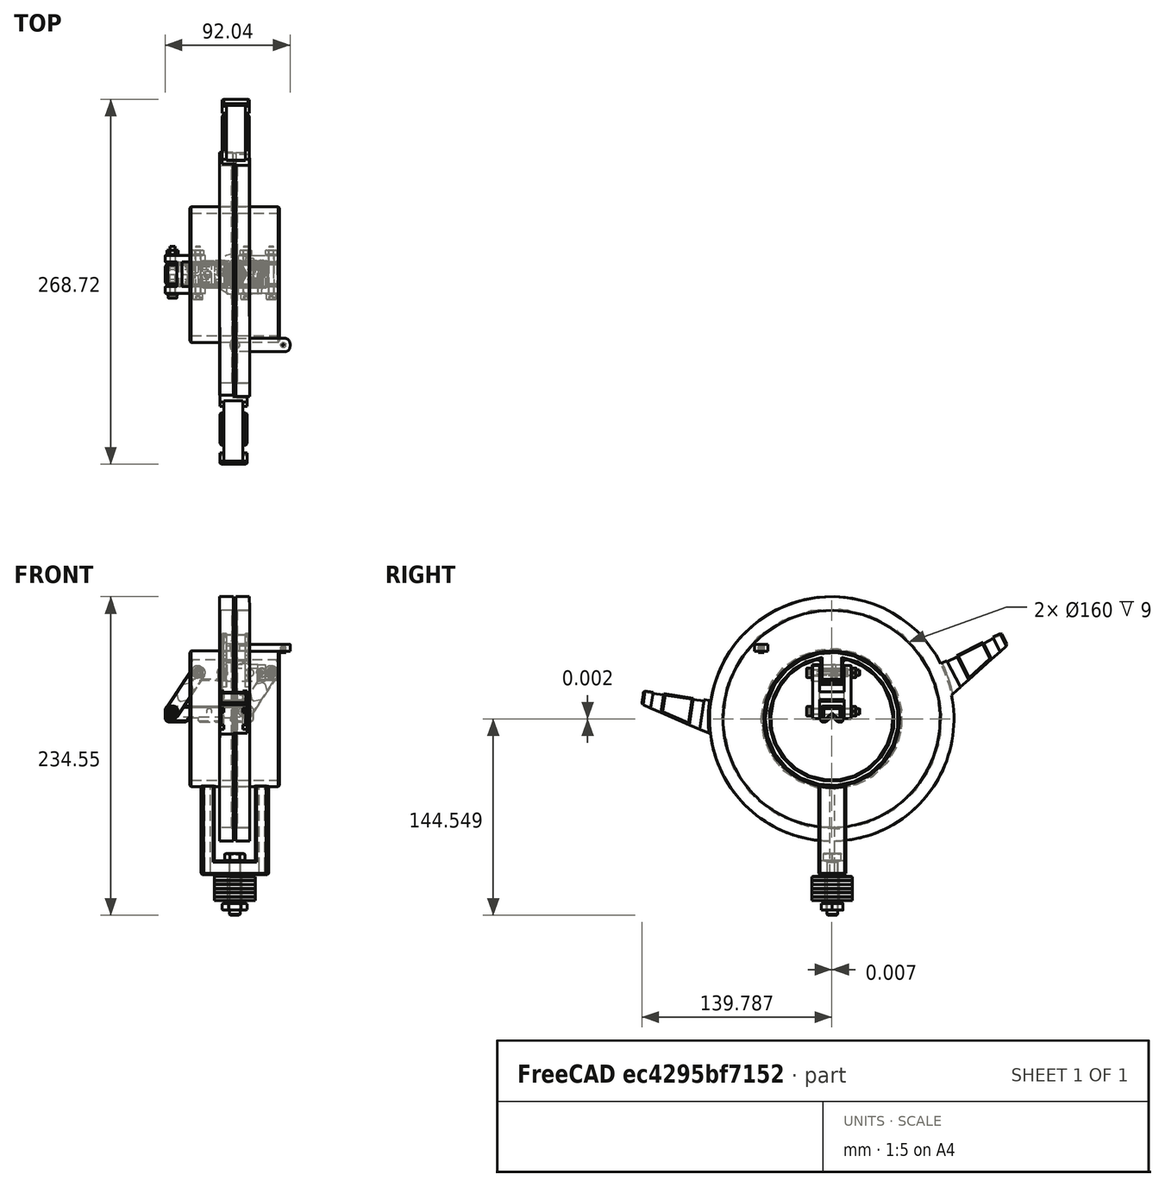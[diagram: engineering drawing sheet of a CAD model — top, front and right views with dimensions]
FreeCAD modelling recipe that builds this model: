
FCSTD DOCUMENT  (FreeCAD 0.18.3R)
Label: assenmbly
License: All rights reserved
LicenseURL: http://en.wikipedia.org/wiki/All_rights_reserved
objects: Part::FeaturePython×45, App::FeaturePython×40
note: 45 computed .brp shape members not serialized (recipe doc carries the construction recipe); baked Part::Feature solids carry a one-line shape summary decoded from their .brp

FEATURE [Part::FeaturePython] b_schlitten_001_  label="schlitten_001"  # a2plus imported part (geometry in sourceFile) (typed FeaturePython)
  Placement = pos=(-61.9458,5.97392,0.234447) rot=(0,0,1;0rad)
  a2p_Version = V0.1
  fixedPosition = true
  sourceFile = ./schlitten.FCStd
  subassemblyImport = false
  timeLastImport = 1.57901e+09
  updateColors = true
FEATURE [Part::FeaturePython] b_hinge_001_  label="hinge_001"  # a2plus imported part (geometry in sourceFile) (typed FeaturePython)
  Placement = pos=(-83.7786,5.97392,25.1844) rot=(-0.66073,0.66073,-0.356189;2.45724rad)
  a2p_Version = V0.1
  fixedPosition = false
  sourceFile = ./hinge.FCStd
  subassemblyImport = false
  timeLastImport = 1.57901e+09
  updateColors = true
FEATURE [Part::FeaturePython] b_uscheibe_001_  label="uscheibe_001"  # a2plus imported part (geometry in sourceFile) (typed FeaturePython)
  Placement = pos=(-34.9458,14.9739,8.23445) rot=(1,0,0;1.5708rad)
  a2p_Version = V0.1
  fixedPosition = false
  sourceFile = ./uscheibe.FCStd
  subassemblyImport = false
  timeLastImport = 1.57901e+09
  updateColors = true
FEATURE [Part::FeaturePython] b_uscheibe_001_001  label="uscheibe_002"  # a2plus imported part (geometry in sourceFile) (typed FeaturePython)
  Placement = pos=(-88.9458,14.9739,8.23445) rot=(0.998298,0.041235,-0.041235;1.5725rad)
  a2p_Version = V0.1
  fixedPosition = false
  sourceFile = ./uscheibe.FCStd
  subassemblyImport = false
  timeLastImport = 1.57901e+09
  updateColors = true
FEATURE [App::FeaturePython] circularEdge_001  label="circularEdge_001__schlitten_001"  # a2plus constraint (typed FeaturePython)
  Object1 = b_uscheibe_001_001
  Object2 = b_schlitten_001_
  ParentTreeObject = -> b_uscheibe_001_001
  SubElement1 = Edge6
  SubElement2 = Edge59
  Type = circularEdge
  directionConstraint = 1
  lockRotation = false
  offset = 0
FEATURE [App::FeaturePython] circularEdge_001_mirror  label="circularEdge_001__uscheibe_002"  # a2plus constraint (typed FeaturePython)
  Object1 = b_uscheibe_001_001
  Object2 = b_schlitten_001_
  ParentTreeObject = -> b_schlitten_001_
  SubElement1 = Edge6
  SubElement2 = Edge59
  Type = circularEdge
  directionConstraint = 1
  lockRotation = false
  offset = 0
FEATURE [App::FeaturePython] circularEdge_002  label="circularEdge_002__uscheibe_002"  # a2plus constraint (typed FeaturePython)
  Object1 = b_hinge_001_
  Object2 = b_uscheibe_001_001
  ParentTreeObject = -> b_hinge_001_
  SubElement1 = Edge11
  SubElement2 = Edge5
  Type = circularEdge
  directionConstraint = 0
  lockRotation = false
  offset = 0
FEATURE [App::FeaturePython] circularEdge_002_mirror  label="circularEdge_002__hinge_001"  # a2plus constraint (typed FeaturePython)
  Object1 = b_hinge_001_
  Object2 = b_uscheibe_001_001
  ParentTreeObject = -> b_uscheibe_001_001
  SubElement1 = Edge11
  SubElement2 = Edge5
  Type = circularEdge
  directionConstraint = 0
  lockRotation = false
  offset = 0
FEATURE [App::FeaturePython] circularEdge_003  label="circularEdge_003__schlitten_001"  # a2plus constraint (typed FeaturePython)
  Object1 = b_uscheibe_001_
  Object2 = b_schlitten_001_
  ParentTreeObject = -> b_uscheibe_001_
  SubElement1 = Edge6
  SubElement2 = Edge63
  Type = circularEdge
  directionConstraint = 1
  lockRotation = false
  offset = 0
FEATURE [App::FeaturePython] circularEdge_003_mirror  label="circularEdge_003__uscheibe_001"  # a2plus constraint (typed FeaturePython)
  Object1 = b_uscheibe_001_
  Object2 = b_schlitten_001_
  ParentTreeObject = -> b_schlitten_001_
  SubElement1 = Edge6
  SubElement2 = Edge63
  Type = circularEdge
  directionConstraint = 1
  lockRotation = false
  offset = 0
FEATURE [Part::FeaturePython] b_uscheibe_001_002  label="uscheibe_003"  # a2plus imported part (geometry in sourceFile) (typed FeaturePython)
  Placement = pos=(-34.9458,-2.02608,8.23445) rot=(0.996711,-0.057304,0.057304;1.57409rad)
  a2p_Version = V0.1
  fixedPosition = false
  sourceFile = ./uscheibe.FCStd
  subassemblyImport = false
  timeLastImport = 1.57901e+09
  updateColors = true
FEATURE [Part::FeaturePython] b_uscheibe_001_003  label="uscheibe_004"  # a2plus imported part (geometry in sourceFile) (typed FeaturePython)
  Placement = pos=(-88.9458,-2.02608,8.23445) rot=(1,0,0;1.5708rad)
  a2p_Version = V0.1
  fixedPosition = false
  sourceFile = ./uscheibe.FCStd
  subassemblyImport = false
  timeLastImport = 1.57901e+09
  updateColors = true
FEATURE [App::FeaturePython] circularEdge_004  label="circularEdge_004__schlitten_001"  # a2plus constraint (typed FeaturePython)
  Object1 = b_uscheibe_001_003
  Object2 = b_schlitten_001_
  ParentTreeObject = -> b_uscheibe_001_003
  SubElement1 = Edge5
  SubElement2 = Edge15
  Type = circularEdge
  directionConstraint = 1
  lockRotation = false
  offset = 0
FEATURE [App::FeaturePython] circularEdge_004_mirror  label="circularEdge_004__uscheibe_004"  # a2plus constraint (typed FeaturePython)
  Object1 = b_uscheibe_001_003
  Object2 = b_schlitten_001_
  ParentTreeObject = -> b_schlitten_001_
  SubElement1 = Edge5
  SubElement2 = Edge15
  Type = circularEdge
  directionConstraint = 1
  lockRotation = false
  offset = 0
FEATURE [App::FeaturePython] circularEdge_005  label="circularEdge_005__schlitten_001"  # a2plus constraint (typed FeaturePython)
  Object1 = b_uscheibe_001_002
  Object2 = b_schlitten_001_
  ParentTreeObject = -> b_uscheibe_001_002
  SubElement1 = Edge5
  SubElement2 = Edge17
  Type = circularEdge
  directionConstraint = 1
  lockRotation = false
  offset = 0
FEATURE [App::FeaturePython] circularEdge_005_mirror  label="circularEdge_005__uscheibe_003"  # a2plus constraint (typed FeaturePython)
  Object1 = b_uscheibe_001_002
  Object2 = b_schlitten_001_
  ParentTreeObject = -> b_schlitten_001_
  SubElement1 = Edge5
  SubElement2 = Edge17
  Type = circularEdge
  directionConstraint = 1
  lockRotation = false
  offset = 0
FEATURE [Part::FeaturePython] b_hinge_001_001  label="hinge_002"  # a2plus imported part (geometry in sourceFile) (typed FeaturePython)
  Placement = pos=(-21.4247,5.97392,19.6879) rot=(0.428706,-0.428706,-0.79525;1.79792rad)
  a2p_Version = V0.1
  fixedPosition = false
  sourceFile = ./hinge.FCStd
  subassemblyImport = false
  timeLastImport = 1.57901e+09
  updateColors = true
FEATURE [App::FeaturePython] circularEdge_006  label="circularEdge_006__uscheibe_003"  # a2plus constraint (typed FeaturePython)
  Object1 = b_hinge_001_001
  Object2 = b_uscheibe_001_002
  ParentTreeObject = -> b_hinge_001_001
  SubElement1 = Edge84
  SubElement2 = Edge6
  Type = circularEdge
  directionConstraint = 0
  lockRotation = false
  offset = 0
FEATURE [App::FeaturePython] circularEdge_006_mirror  label="circularEdge_006__hinge_002"  # a2plus constraint (typed FeaturePython)
  Object1 = b_hinge_001_001
  Object2 = b_uscheibe_001_002
  ParentTreeObject = -> b_uscheibe_001_002
  SubElement1 = Edge84
  SubElement2 = Edge6
  Type = circularEdge
  directionConstraint = 0
  lockRotation = false
  offset = 0
FEATURE [Part::FeaturePython] b_uscheibe_001_004  label="uscheibe_005"  # a2plus imported part (geometry in sourceFile) (typed FeaturePython)
  Placement = pos=(-70.2575,13.9739,36.6378) rot=(-0.243331,0.685853,0.685853;2.66421rad)
  a2p_Version = V0.1
  fixedPosition = false
  sourceFile = ./uscheibe.FCStd
  subassemblyImport = false
  timeLastImport = 1.57901e+09
  updateColors = true
FEATURE [Part::FeaturePython] b_uscheibe_001_005  label="uscheibe_006"  # a2plus imported part (geometry in sourceFile) (typed FeaturePython)
  Placement = pos=(-16.2575,13.9739,36.6378) rot=(0.393172,0.65016,0.65016;3.89081rad)
  a2p_Version = V0.1
  fixedPosition = false
  sourceFile = ./uscheibe.FCStd
  subassemblyImport = false
  timeLastImport = 1.57901e+09
  updateColors = true
FEATURE [Part::FeaturePython] b_uscheibe_001_006  label="uscheibe_007"  # a2plus imported part (geometry in sourceFile) (typed FeaturePython)
  Placement = pos=(-70.2575,-2.02608,36.6378) rot=(0.99737,0.051246,-0.051246;1.57343rad)
  a2p_Version = V0.1
  fixedPosition = false
  sourceFile = ./uscheibe.FCStd
  subassemblyImport = false
  timeLastImport = 1.57901e+09
  updateColors = true
FEATURE [Part::FeaturePython] b_uscheibe_001_007  label="uscheibe_008"  # a2plus imported part (geometry in sourceFile) (typed FeaturePython)
  Placement = pos=(-16.2575,-2.02608,36.6378) rot=(0.996759,-0.056884,0.056884;1.57404rad)
  a2p_Version = V0.1
  fixedPosition = false
  sourceFile = ./uscheibe.FCStd
  subassemblyImport = false
  timeLastImport = 1.57901e+09
  updateColors = true
FEATURE [App::FeaturePython] circularEdge_007  label="circularEdge_007__hinge_001"  # a2plus constraint (typed FeaturePython)
  Object1 = b_uscheibe_001_004
  Object2 = b_hinge_001_
  ParentTreeObject = -> b_uscheibe_001_004
  SubElement1 = Edge6
  SubElement2 = Edge67
  Type = circularEdge
  directionConstraint = 1
  lockRotation = false
  offset = 0
FEATURE [App::FeaturePython] circularEdge_007_mirror  label="circularEdge_007__uscheibe_005"  # a2plus constraint (typed FeaturePython)
  Object1 = b_uscheibe_001_004
  Object2 = b_hinge_001_
  ParentTreeObject = -> b_hinge_001_
  SubElement1 = Edge6
  SubElement2 = Edge67
  Type = circularEdge
  directionConstraint = 1
  lockRotation = false
  offset = 0
FEATURE [App::FeaturePython] circularEdge_008  label="circularEdge_008__hinge_002"  # a2plus constraint (typed FeaturePython)
  Object1 = b_uscheibe_001_005
  Object2 = b_hinge_001_001
  ParentTreeObject = -> b_uscheibe_001_005
  SubElement1 = Edge6
  SubElement2 = Edge11
  Type = circularEdge
  directionConstraint = 1
  lockRotation = false
  offset = 0
FEATURE [App::FeaturePython] circularEdge_008_mirror  label="circularEdge_008__uscheibe_006"  # a2plus constraint (typed FeaturePython)
  Object1 = b_uscheibe_001_005
  Object2 = b_hinge_001_001
  ParentTreeObject = -> b_hinge_001_001
  SubElement1 = Edge6
  SubElement2 = Edge11
  Type = circularEdge
  directionConstraint = 1
  lockRotation = false
  offset = 0
FEATURE [App::FeaturePython] circularEdge_009  label="circularEdge_009__hinge_001"  # a2plus constraint (typed FeaturePython)
  Object1 = b_uscheibe_001_006
  Object2 = b_hinge_001_
  ParentTreeObject = -> b_uscheibe_001_006
  SubElement1 = Edge6
  SubElement2 = Edge84
  Type = circularEdge
  directionConstraint = 0
  lockRotation = false
  offset = 0
FEATURE [App::FeaturePython] circularEdge_009_mirror  label="circularEdge_009__uscheibe_007"  # a2plus constraint (typed FeaturePython)
  Object1 = b_uscheibe_001_006
  Object2 = b_hinge_001_
  ParentTreeObject = -> b_hinge_001_
  SubElement1 = Edge6
  SubElement2 = Edge84
  Type = circularEdge
  directionConstraint = 0
  lockRotation = false
  offset = 0
FEATURE [App::FeaturePython] circularEdge_010  label="circularEdge_010__hinge_002"  # a2plus constraint (typed FeaturePython)
  Object1 = b_uscheibe_001_007
  Object2 = b_hinge_001_001
  ParentTreeObject = -> b_uscheibe_001_007
  SubElement1 = Edge6
  SubElement2 = Edge61
  Type = circularEdge
  directionConstraint = 0
  lockRotation = false
  offset = 0
FEATURE [App::FeaturePython] circularEdge_010_mirror  label="circularEdge_010__uscheibe_008"  # a2plus constraint (typed FeaturePython)
  Object1 = b_uscheibe_001_007
  Object2 = b_hinge_001_001
  ParentTreeObject = -> b_hinge_001_001
  SubElement1 = Edge6
  SubElement2 = Edge61
  Type = circularEdge
  directionConstraint = 0
  lockRotation = false
  offset = 0
FEATURE [Part::FeaturePython] b_gondel_001_  label="gondel_001"  # a2plus imported part (geometry in sourceFile) (typed FeaturePython)
  Placement = pos=(-43.2575,5.87277,2.6378) rot=(0.57735,-0.57735,-0.57735;2.0944rad)
  a2p_Version = V0.1
  fixedPosition = false
  sourceFile = ./gondel.FCStd
  subassemblyImport = false
  timeLastImport = 1.57901e+09
  updateColors = true
FEATURE [App::FeaturePython] circularEdge_011  label="circularEdge_011__gondel_001"  # a2plus constraint (typed FeaturePython)
  Object1 = b_uscheibe_001_006
  Object2 = b_gondel_001_
  ParentTreeObject = -> b_uscheibe_001_006
  SubElement1 = Edge5
  SubElement2 = Edge68
  Type = circularEdge
  directionConstraint = 0
  lockRotation = false
  offset = 0
FEATURE [App::FeaturePython] circularEdge_011_mirror  label="circularEdge_011__uscheibe_007"  # a2plus constraint (typed FeaturePython)
  Object1 = b_uscheibe_001_006
  Object2 = b_gondel_001_
  ParentTreeObject = -> b_gondel_001_
  SubElement1 = Edge5
  SubElement2 = Edge68
  Type = circularEdge
  directionConstraint = 0
  lockRotation = false
  offset = 0
FEATURE [App::FeaturePython] circularEdge_012  label="circularEdge_012__uscheibe_008"  # a2plus constraint (typed FeaturePython)
  Object1 = b_gondel_001_
  Object2 = b_uscheibe_001_007
  ParentTreeObject = -> b_gondel_001_
  SubElement1 = Edge66
  SubElement2 = Edge5
  Type = circularEdge
  directionConstraint = 0
  lockRotation = false
  offset = 0
FEATURE [App::FeaturePython] circularEdge_012_mirror  label="circularEdge_012__gondel_001"  # a2plus constraint (typed FeaturePython)
  Object1 = b_gondel_001_
  Object2 = b_uscheibe_001_007
  ParentTreeObject = -> b_uscheibe_001_007
  SubElement1 = Edge66
  SubElement2 = Edge5
  Type = circularEdge
  directionConstraint = 0
  lockRotation = false
  offset = 0
FEATURE [App::FeaturePython] circularEdge_013  label="circularEdge_013__uscheibe_008"  # a2plus constraint (typed FeaturePython)
  Object1 = b_hinge_001_001
  Object2 = b_uscheibe_001_007
  ParentTreeObject = -> b_hinge_001_001
  SubElement1 = Edge61
  SubElement2 = Edge6
  Type = circularEdge
  directionConstraint = 0
  lockRotation = false
  offset = 0
FEATURE [App::FeaturePython] circularEdge_013_mirror  label="circularEdge_013__hinge_002"  # a2plus constraint (typed FeaturePython)
  Object1 = b_hinge_001_001
  Object2 = b_uscheibe_001_007
  ParentTreeObject = -> b_uscheibe_001_007
  SubElement1 = Edge61
  SubElement2 = Edge6
  Type = circularEdge
  directionConstraint = 0
  lockRotation = false
  offset = 0
FEATURE [Part::FeaturePython] b_servo_001_  label="servo_001"  # a2plus imported part (geometry in sourceFile) (typed FeaturePython)
  Placement = pos=(-32.0813,-8.31554,36.6357) rot=(-0.99997,-0.005509,0.005531;1.5707rad)
  a2p_Version = V0.1
  fixedPosition = false
  sourceFile = ./servo.FCStd
  subassemblyImport = false
  timeLastImport = 1.57901e+09
  updateColors = true
FEATURE [App::FeaturePython] circularEdge_014  label="circularEdge_014__gondel_001"  # a2plus constraint (typed FeaturePython)
  Object1 = b_servo_001_
  Object2 = b_gondel_001_
  ParentTreeObject = -> b_servo_001_
  SubElement1 = Edge64
  SubElement2 = Edge137
  Type = circularEdge
  directionConstraint = 1
  lockRotation = false
  offset = 0
FEATURE [App::FeaturePython] circularEdge_014_mirror  label="circularEdge_014__servo_001"  # a2plus constraint (typed FeaturePython)
  Object1 = b_servo_001_
  Object2 = b_gondel_001_
  ParentTreeObject = -> b_gondel_001_
  SubElement1 = Edge64
  SubElement2 = Edge137
  Type = circularEdge
  directionConstraint = 1
  lockRotation = false
  offset = 0
FEATURE [App::FeaturePython] circularEdge_015  label="circularEdge_015__servo_001"  # a2plus constraint (typed FeaturePython)
  Object1 = b_gondel_001_
  Object2 = b_servo_001_
  ParentTreeObject = -> b_gondel_001_
  SubElement1 = Edge106
  SubElement2 = Edge58
  Type = circularEdge
  directionConstraint = 1
  lockRotation = false
  offset = 0
FEATURE [App::FeaturePython] circularEdge_015_mirror  label="circularEdge_015__gondel_001"  # a2plus constraint (typed FeaturePython)
  Object1 = b_gondel_001_
  Object2 = b_servo_001_
  ParentTreeObject = -> b_servo_001_
  SubElement1 = Edge106
  SubElement2 = Edge58
  Type = circularEdge
  directionConstraint = 1
  lockRotation = false
  offset = 0
FEATURE [Part::FeaturePython] Washer002  label="M4-Washer105"  # Fasteners workbench fastener (typed FeaturePython)
  Placement = pos=(-88.9458,-8.02608,8.23445) rot=(1,0,0;1.5708rad)
  baseObject = -> b_hinge_001_ [Edge77]
  diameter = 5
  invert = false
  matchOuter = false
  offset = 0
  type = 2
FEATURE [Part::FeaturePython] Washer003  label="M4-Washer103"  # Fasteners workbench fastener (typed FeaturePython)
  Placement = pos=(-34.9458,-8.02608,8.23445) rot=(1,0,0;1.5708rad)
  baseObject = -> b_hinge_001_001 [Edge78]
  diameter = 5
  invert = false
  matchOuter = false
  offset = 0
  type = 2
FEATURE [Part::FeaturePython] Washer004  label="M4-Washer100"  # Fasteners workbench fastener (typed FeaturePython)
  Placement = pos=(-88.9458,19.9739,8.23445) rot=(-1,0,0;1.5708rad)
  baseObject = -> b_hinge_001_ [Edge51]
  diameter = 5
  invert = true
  matchOuter = false
  offset = 0
  type = 2
FEATURE [Part::FeaturePython] Washer005  label="M4-Washer102"  # Fasteners workbench fastener (typed FeaturePython)
  Placement = pos=(-34.9458,19.9739,8.23445) rot=(-1,0,0;1.5708rad)
  baseObject = -> b_hinge_001_001 [Edge55]
  diameter = 5
  invert = true
  matchOuter = false
  offset = 0
  type = 2
FEATURE [Part::FeaturePython] Washer  label="M4-Washer101"  # Fasteners workbench fastener (typed FeaturePython)
  Placement = pos=(-16.2575,19.9739,36.6378) rot=(-1,0,0;1.5708rad)
  baseObject = -> b_hinge_001_001 [Edge51]
  diameter = 5
  invert = true
  matchOuter = false
  offset = 0
  type = 2
FEATURE [Part::FeaturePython] Washer006  label="M4-Washer099"  # Fasteners workbench fastener (typed FeaturePython)
  Placement = pos=(-70.2575,19.9739,36.6378) rot=(-1,0,0;1.5708rad)
  baseObject = -> b_hinge_001_ [Edge55]
  diameter = 5
  invert = true
  matchOuter = false
  offset = 0
  type = 2
FEATURE [Part::FeaturePython] Washer007  label="M4-Washer"  # Fasteners workbench fastener (typed FeaturePython)
  Placement = pos=(-16.2575,-8.02608,36.6378) rot=(1,0,0;1.5708rad)
  baseObject = -> b_hinge_001_001 [Edge77]
  diameter = 5
  invert = false
  matchOuter = false
  offset = 0
  type = 2
FEATURE [Part::FeaturePython] Washer008  label="M4-Washer104"  # Fasteners workbench fastener (typed FeaturePython)
  Placement = pos=(-70.2575,-8.02608,36.6378) rot=(1,0,0;1.5708rad)
  baseObject = -> b_hinge_001_ [Edge78]
  diameter = 5
  invert = false
  matchOuter = false
  offset = 0
  type = 2
FEATURE [Part::FeaturePython] Screw  label="M4x35-Screw045"  # Fasteners workbench fastener (typed FeaturePython)
  Placement = pos=(-88.9458,-8.57608,8.23445) rot=(1,0,0;1.5708rad)
  baseObject = -> Washer002 [Edge1]
  diameter = 5
  invert = false
  length = 10
  matchOuter = false
  offset = 0
  thread = false
  type = 6
FEATURE [Part::FeaturePython] Screw001  label="M4x35-Screw044"  # Fasteners workbench fastener (typed FeaturePython)
  Placement = pos=(-70.2575,-8.57608,36.6378) rot=(1,0,0;1.5708rad)
  baseObject = -> Washer008 [Edge1]
  diameter = 4
  invert = false
  length = 8
  matchOuter = false
  offset = 0
  thread = false
  type = 5
FEATURE [Part::FeaturePython] Screw002  label="M4x35-Screw"  # Fasteners workbench fastener (typed FeaturePython)
  Placement = pos=(-34.9458,-8.57608,8.23445) rot=(1,0,0;1.5708rad)
  baseObject = -> Washer003 [Edge1]
  diameter = 4
  invert = false
  length = 8
  matchOuter = false
  offset = 0
  thread = false
  type = 5
FEATURE [Part::FeaturePython] Screw003  label="M4x35-Screw043"  # Fasteners workbench fastener (typed FeaturePython)
  Placement = pos=(-16.2575,-8.57608,36.6378) rot=(1,0,0;1.5708rad)
  baseObject = -> Washer007 [Edge1]
  diameter = 4
  invert = false
  length = 8
  matchOuter = false
  offset = 0
  thread = false
  type = 5
FEATURE [Part::FeaturePython] Nut  label="M4-Nut"  # Fasteners workbench fastener (typed FeaturePython)
  Placement = pos=(-34.9458,20.5239,8.23445) rot=(-1,0,0;1.5708rad)
  baseObject = -> Washer005 [Edge1]
  diameter = 6
  invert = false
  matchOuter = false
  offset = 0
  thread = false
  type = 4
FEATURE [Part::FeaturePython] Nut001  label="M4-Nut045"  # Fasteners workbench fastener (typed FeaturePython)
  Placement = pos=(-16.2575,20.5239,36.6378) rot=(-1,0,0;1.5708rad)
  baseObject = -> Washer [Edge1]
  diameter = 6
  invert = false
  matchOuter = false
  offset = 0
  thread = false
  type = 4
FEATURE [Part::FeaturePython] Nut002  label="M4-Nut044"  # Fasteners workbench fastener (typed FeaturePython)
  Placement = pos=(-88.9458,20.5239,8.23445) rot=(-1,0,0;1.5708rad)
  baseObject = -> Washer004 [Edge1]
  diameter = 6
  invert = false
  matchOuter = false
  offset = 0
  thread = false
  type = 4
FEATURE [Part::FeaturePython] Nut003  label="M4-Nut043"  # Fasteners workbench fastener (typed FeaturePython)
  Placement = pos=(-70.2575,20.5239,36.6378) rot=(-1,0,0;1.5708rad)
  baseObject = -> Washer006 [Edge1]
  diameter = 6
  invert = false
  matchOuter = false
  offset = 0
  thread = false
  type = 4
FEATURE [Part::FeaturePython] Screw004  label="M3x4-Screw"  # Fasteners workbench fastener (typed FeaturePython)
  Placement = pos=(-52.2575,13.9739,36.6378) rot=(-1,0,0;1.5708rad)
  baseObject = -> b_gondel_001_ [Edge48]
  diameter = 1
  invert = true
  length = 0
  matchOuter = false
  offset = 0
  thread = false
  type = 0
FEATURE [Part::FeaturePython] Screw005  label="M3x4-Screw001"  # Fasteners workbench fastener (typed FeaturePython)
  Placement = pos=(-23.2575,13.9739,36.6378) rot=(-1,0,0;1.5708rad)
  baseObject = -> b_gondel_001_ [Edge46]
  diameter = 1
  invert = true
  length = 0
  matchOuter = false
  offset = 0
  thread = false
  type = 0
FEATURE [Part::FeaturePython] b_rotor_001_  label="rotor_001"  # a2plus imported part (geometry in sourceFile) (typed FeaturePython)
  Placement = pos=(-24.4097,-46.0942,52.5618) rot=(0,0,1;0rad)
  a2p_Version = V0.1
  fixedPosition = false
  sourceFile = ./rotor.FCStd
  subassemblyImport = false
  timeLastImport = 1.57901e+09
  updateColors = true
FEATURE [Part::FeaturePython] b_lager_001_  label="lager_001"  # a2plus imported part (geometry in sourceFile) (typed FeaturePython)
  Placement = pos=(16.7425,5.87277,2.6378) rot=(-0.570077,0.591629,-0.570077;2.07311rad)
  a2p_Version = V0.1
  fixedPosition = false
  sourceFile = ./lager.FCStd
  subassemblyImport = false
  timeLastImport = 1.579e+09
  updateColors = true
FEATURE [App::FeaturePython] circularEdge_016  label="circularEdge_016__gondel_001"  # a2plus constraint (typed FeaturePython)
  Object1 = b_lager_001_
  Object2 = b_gondel_001_
  ParentTreeObject = -> b_lager_001_
  SubElement1 = Edge8
  SubElement2 = Edge2
  Type = circularEdge
  directionConstraint = 1
  lockRotation = false
  offset = 0
FEATURE [App::FeaturePython] circularEdge_016_mirror  label="circularEdge_016__lager_001"  # a2plus constraint (typed FeaturePython)
  Object1 = b_lager_001_
  Object2 = b_gondel_001_
  ParentTreeObject = -> b_gondel_001_
  SubElement1 = Edge8
  SubElement2 = Edge2
  Type = circularEdge
  directionConstraint = 1
  lockRotation = false
  offset = 0
FEATURE [Part::FeaturePython] b_lager_001_001  label="lager_002"  # a2plus imported part (geometry in sourceFile) (typed FeaturePython)
  Placement = pos=(4.74247,5.87277,2.6378) rot=(-0.570077,0.591629,-0.570077;2.07311rad)
  a2p_Version = V0.1
  fixedPosition = false
  sourceFile = ./lager.FCStd
  subassemblyImport = false
  timeLastImport = 1.579e+09
  updateColors = true
FEATURE [App::FeaturePython] circularEdge_017  label="circularEdge_017__lager_002"  # a2plus constraint (typed FeaturePython)
  Object1 = b_gondel_001_
  Object2 = b_lager_001_001
  ParentTreeObject = -> b_gondel_001_
  SubElement1 = Edge12
  SubElement2 = Edge9
  Type = circularEdge
  directionConstraint = 1
  lockRotation = false
  offset = 0
FEATURE [App::FeaturePython] circularEdge_017_mirror  label="circularEdge_017__gondel_001"  # a2plus constraint (typed FeaturePython)
  Object1 = b_gondel_001_
  Object2 = b_lager_001_001
  ParentTreeObject = -> b_lager_001_001
  SubElement1 = Edge12
  SubElement2 = Edge9
  Type = circularEdge
  directionConstraint = 1
  lockRotation = false
  offset = 0
FEATURE [Part::FeaturePython] b_fluegel_001_  label="fluegel_001"  # a2plus imported part (geometry in sourceFile) (typed FeaturePython)
  Placement = pos=(-32.2575,5.87508,2.64019) rot=(-0.648745,0.398243,0.648485;3.89967rad)
  a2p_Version = V0.1
  fixedPosition = false
  sourceFile = ./fluegel.FCStd
  subassemblyImport = false
  timeLastImport = 1.57902e+09
  updateColors = true
FEATURE [App::FeaturePython] circularEdge_018  label="circularEdge_018__lager_001"  # a2plus constraint (typed FeaturePython)
  Object1 = b_fluegel_001_
  Object2 = b_lager_001_
  ParentTreeObject = -> b_fluegel_001_
  SubElement1 = Edge152
  SubElement2 = Edge2
  Type = circularEdge
  directionConstraint = 1
  lockRotation = false
  offset = 0
FEATURE [App::FeaturePython] circularEdge_018_mirror  label="circularEdge_018__fluegel_001"  # a2plus constraint (typed FeaturePython)
  Object1 = b_fluegel_001_
  Object2 = b_lager_001_
  ParentTreeObject = -> b_lager_001_
  SubElement1 = Edge152
  SubElement2 = Edge2
  Type = circularEdge
  directionConstraint = 1
  lockRotation = false
  offset = 0
FEATURE [Part::FeaturePython] b_fluegel_001_001  label="fluegel_002"  # a2plus imported part (geometry in sourceFile) (typed FeaturePython)
  Placement = pos=(-54.258,5.86198,2.6434) rot=(-0.545997,-0.635085,-0.546401;4.27173rad)
  a2p_Version = V0.1
  fixedPosition = false
  sourceFile = ./fluegel.FCStd
  subassemblyImport = false
  timeLastImport = 1.57902e+09
  updateColors = true
FEATURE [App::FeaturePython] circularEdge_019  label="circularEdge_019__lager_002"  # a2plus constraint (typed FeaturePython)
  Object1 = b_fluegel_001_001
  Object2 = b_lager_001_001
  ParentTreeObject = -> b_fluegel_001_001
  SubElement1 = Edge152
  SubElement2 = Edge3
  Type = circularEdge
  directionConstraint = 0
  lockRotation = false
  offset = 0
FEATURE [App::FeaturePython] circularEdge_019_mirror  label="circularEdge_019__fluegel_002"  # a2plus constraint (typed FeaturePython)
  Object1 = b_fluegel_001_001
  Object2 = b_lager_001_001
  ParentTreeObject = -> b_lager_001_001
  SubElement1 = Edge152
  SubElement2 = Edge3
  Type = circularEdge
  directionConstraint = 0
  lockRotation = false
  offset = 0
FEATURE [Part::FeaturePython] b_waage_001_  label="waage_001"  # a2plus imported part (geometry in sourceFile) (typed FeaturePython)
  Placement = pos=(-42.9356,6.17693,3.09831) rot=(0,1,0;1.57234rad)
  a2p_Version = V0.1
  fixedPosition = false
  sourceFile = ./waage.FCStd
  subassemblyImport = false
  timeLastImport = 1.57925e+09
  updateColors = true
FEATURE [App::FeaturePython] axisParallel_001  label="axisParallel_001__gondel_001"  # a2plus constraint (typed FeaturePython)
  Object1 = b_waage_001_
  Object2 = b_gondel_001_
  ParentTreeObject = -> b_waage_001_
  SubElement1 = Face13
  SubElement2 = Face13
  Type = axisParallel
  directionConstraint = 0
FEATURE [App::FeaturePython] axisParallel_001_mirror  label="axisParallel_001__waage_001"  # a2plus constraint (typed FeaturePython)
  Object1 = b_waage_001_
  Object2 = b_gondel_001_
  ParentTreeObject = -> b_gondel_001_
  SubElement1 = Face13
  SubElement2 = Face13
  Type = axisParallel
  directionConstraint = 0
FEATURE [Part::FeaturePython] Screw006  label="M8x40-Screw"  # Fasteners workbench fastener (typed FeaturePython)
  Placement = pos=(-43.0976,6.17693,-101.902) rot=(9e-06,1,0;0.001543rad)
  baseObject = -> b_waage_001_ [Edge5]
  diameter = 9
  invert = false
  length = 5
  matchOuter = false
  offset = 0
  thread = false
  type = 14
FEATURE [Part::FeaturePython] Washer009  label="M10-Washer024"  # Fasteners workbench fastener (typed FeaturePython)
  Placement = pos=(-43.1243,6.17693,-119.152) rot=(9e-06,1,0;0.001543rad)
  baseObject = -> Screw006 [Edge37]
  diameter = 7
  invert = false
  matchOuter = false
  offset = -17
  type = 3
FEATURE [Part::FeaturePython] Washer010  label="M10-Washer"  # Fasteners workbench fastener (typed FeaturePython)
  Placement = pos=(-43.1335,6.17693,-125.135) rot=(9e-06,1,0;0.001543rad)
  baseObject = -> Screw006 [Edge39]
  diameter = 7
  invert = false
  matchOuter = false
  offset = 16
  type = 3
FEATURE [Part::FeaturePython] Washer011  label="M10-Washer023"  # Fasteners workbench fastener (typed FeaturePython)
  Placement = pos=(-43.1196,6.17693,-116.152) rot=(9e-06,1,0;0.001543rad)
  baseObject = -> Screw006 [Edge37]
  diameter = 7
  invert = false
  matchOuter = false
  offset = -14
  type = 3
FEATURE [Part::FeaturePython] Washer012  label="M10-Washer021"  # Fasteners workbench fastener (typed FeaturePython)
  Placement = pos=(-43.1381,6.17693,-128.135) rot=(9e-06,1,0;0.001543rad)
  baseObject = -> Screw006 [Edge39]
  diameter = 7
  invert = false
  matchOuter = false
  offset = 13
  type = 3
FEATURE [Part::FeaturePython] Washer013  label="M10-Washer022"  # Fasteners workbench fastener (typed FeaturePython)
  Placement = pos=(-43.1289,6.17693,-122.152) rot=(9e-06,1,0;0.001543rad)
  baseObject = -> Screw006 [Edge37]
  diameter = 7
  invert = false
  matchOuter = false
  offset = -20
  type = 3
FEATURE [Part::FeaturePython] Washer014  label="M10-Washer020"  # Fasteners workbench fastener (typed FeaturePython)
  Placement = pos=(-43.1427,6.17693,-131.135) rot=(9e-06,1,0;0.001543rad)
  baseObject = -> Screw006 [Edge39]
  diameter = 7
  invert = false
  matchOuter = false
  offset = 10
  type = 3
FEATURE [Part::FeaturePython] Nut004  label="M10-Nut"  # Fasteners workbench fastener (typed FeaturePython)
  Placement = pos=(-43.1536,6.17693,-138.152) rot=(9e-06,1,0;0.001543rad)
  baseObject = -> Screw006 [Edge37]
  diameter = 10
  invert = false
  matchOuter = false
  offset = -36
  thread = false
  type = 6
